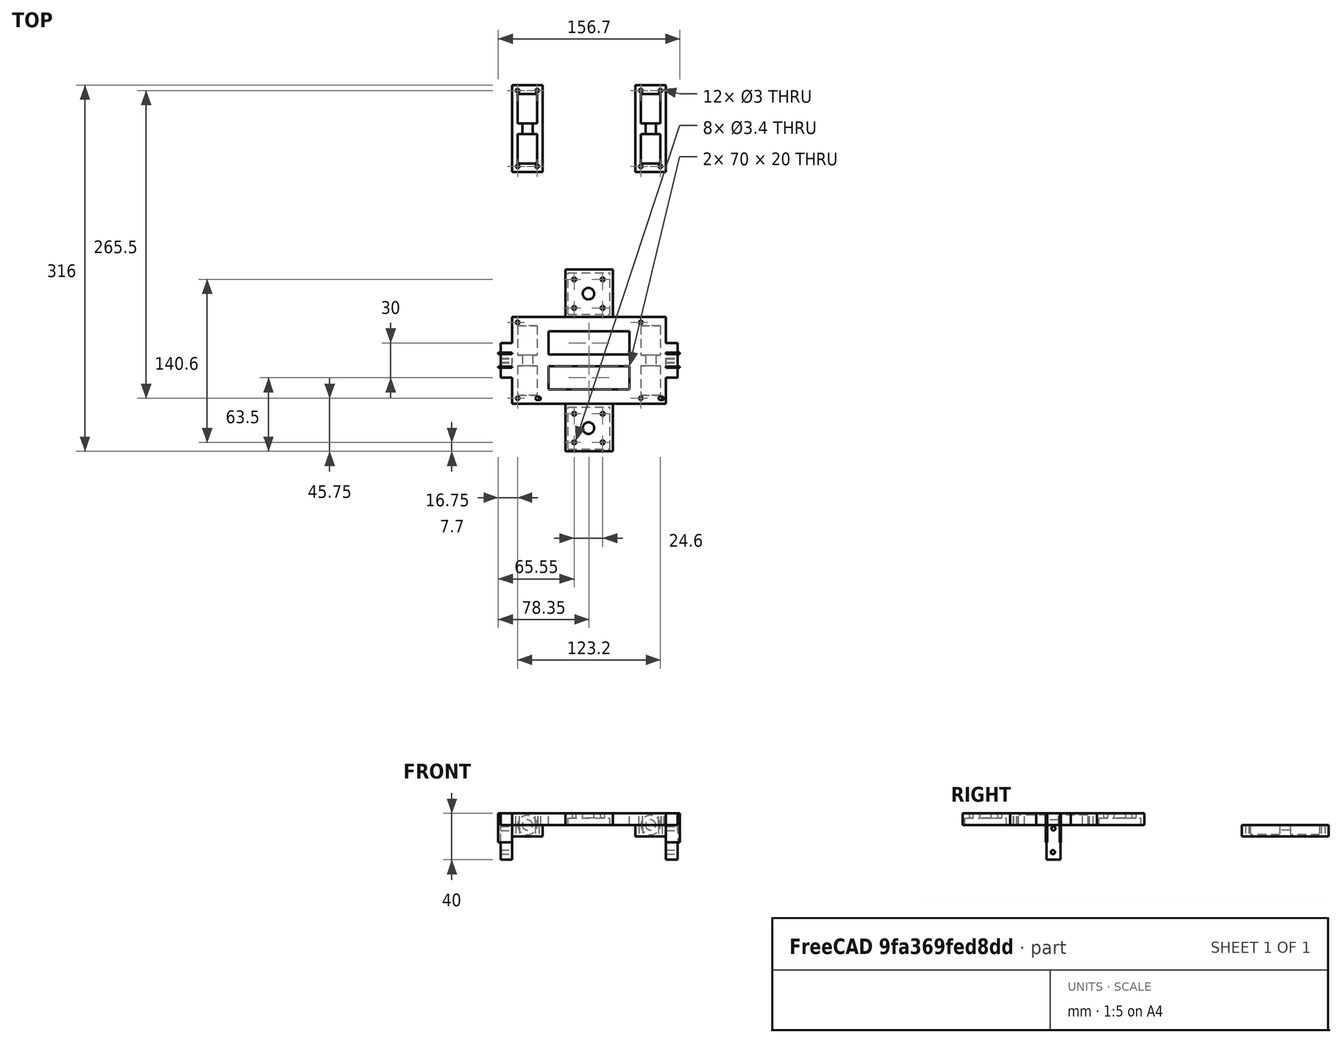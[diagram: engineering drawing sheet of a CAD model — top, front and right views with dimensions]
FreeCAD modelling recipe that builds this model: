
FCSTD DOCUMENT  (FreeCAD 0.16R6712 (Git))
Label: 1
License: All rights reserved
LicenseURL: http://en.wikipedia.org/wiki/All_rights_reserved
objects: Part::Cut×24, Part::Cylinder×21, Part::Box×14, Part::Fuse×5, Part::FeaturePython×4, Part::MultiFuse×3
note: 71 computed .brp shape members not serialized (recipe doc carries the construction recipe); baked Part::Feature solids carry a one-line shape summary decoded from their .brp

FEATURE [Part::Box] Box  label="Cubo"
  Height = 10
  Length = 26.35
  Width = 75
FEATURE [Part::Cylinder] Cylinder  label="Cilindro"
  Angle = 360
  Height = 10
  Placement = pos=(4.75,4.75,0) rot=(0,0,1;0rad)
  Radius = 1.5
FEATURE [Part::Cylinder] Cylinder002  label="Cilindro002"
  Angle = 360
  Height = 10
  Placement = pos=(4.75,70.25,0) rot=(0,0,1;0rad)
  Radius = 1.5
FEATURE [Part::Cylinder] Cylinder003  label="Cilindro003"
  Angle = 360
  Height = 10
  Placement = pos=(23.1425,4.56262,6.40077e-06) rot=(0,0,1;0rad)
  Radius = 1.5
FEATURE [Part::Cut] Cut
  Base = -> Box
  Tool = -> Cylinder
FEATURE [Part::Cut] Cut001
  Base = -> Cut
  Tool = -> Cylinder002
FEATURE [Part::Cut] Cut002
  Base = -> Cut001
  Tool = -> Cylinder003
FEATURE [Part::Cylinder] Cylinder004  label="Cilindro004"
  Angle = 360
  Height = 25.35
  Placement = pos=(13.175,30,0) rot=(1,0,0;1.5708rad)
  Radius = 8.4
FEATURE [Part::Cylinder] Cylinder005  label="Cilindro005"
  Angle = 360
  Height = 25.35
  Placement = pos=(13.175,64.5,0) rot=(1,0,0;1.5708rad)
  Radius = 8.4
FEATURE [Part::Cylinder] Cylinder006  label="Cilindro006"
  Angle = 360
  Height = 9.5
  Placement = pos=(13.175,39.5,0) rot=(1,0,0;1.5708rad)
  Radius = 4.4
FEATURE [Part::Fuse] Fusion
  Base = -> Cylinder004
  Tool = -> Cylinder005
FEATURE [Part::Fuse] Fusion001
  Base = -> Fusion
  Placement = pos=(0,2.75,0) rot=(0,0,1;0rad)
  Tool = -> Cylinder006
FEATURE [Part::Cylinder] Cylinder001  label="Cilindro001"
  Angle = 360
  Height = 10
  Placement = pos=(21.6,4.75,0) rot=(0,0,1;0rad)
  Radius = 1.5
FEATURE [Part::Cut] Cut004
  Base = -> Cut002
  Tool = -> Cylinder001
FEATURE [Part::Cut] Cut003
  Base = -> Cut002
  Tool = -> Cylinder001
FEATURE [Part::Fuse] Fusion002
  Base = -> Cut004
  Tool = -> Cut003
FEATURE [Part::Cut] Cut005
  Base = -> Fusion002
  Tool = -> Fusion001
FEATURE [Part::Cut] Cut006
  Base = -> Cut005
  Tool = -> Cylinder001
FEATURE [Part::FeaturePython] Array  label="Carrileras"  # Draft array (typed FeaturePython)
  Angle = 360
  ArrayType = 0
  Axis = (0,0,1)
  Base = -> Cut006
  Center = (0,0,0)
  Fuse = false
  IntervalAxis = (0,0,0)
  IntervalX = (106.35,0,0)
  IntervalY = (0,1,0)
  IntervalZ = (0,0,0)
  NumberPolar = 1
  NumberX = 2
  NumberY = 1
  NumberZ = 1
FEATURE [Part::Box] Box001  label="Centro"
  Height = 10
  Length = 80
  Placement = pos=(26.35,0,0) rot=(0,0,1;0rad)
  Width = 75
FEATURE [Part::Box] Box002  label="Lucernario"
  Height = 10
  Length = 70
  Placement = pos=(31.35,12.5,0) rot=(0,0,1;0rad)
  Width = 20
FEATURE [Part::Box] Box003  label="Lucernario2"
  Height = 10
  Length = 70
  Placement = pos=(31.35,42.5,0) rot=(0,0,1;0rad)
  Width = 20
FEATURE [Part::Cut] Cut007
  Base = -> Box001
  Tool = -> Box002
FEATURE [Part::Cut] Cut008  label="Centro1"
  Base = -> Cut007
  Tool = -> Box003
FEATURE [Part::Box] Box006  label="Guia1"
  Height = 10
  Length = 10
  Placement = pos=(-10,22.5,0) rot=(0,0,1;0rad)
  Width = 30
FEATURE [Part::Box] Box007  label="Guia2"
  Height = 10
  Length = 10
  Placement = pos=(132.7,22.5,0) rot=(0,0,1;0rad)
  Width = 30
FEATURE [Part::Fuse] Fusion005
  Base = -> Array
  Tool = -> Box006
FEATURE [Part::MultiFuse] Fusion006  label="Carrileras y guias"
  Shapes = -> [Fusion005,Box007]
FEATURE [Part::Box] Box010  label="Cubo003"
  Height = 10
  Length = 26.35
  Width = 75
FEATURE [Part::Cylinder] Cylinder007  label="Cilindro007"
  Angle = 360
  Height = 25.35
  Placement = pos=(13.175,67.25,0) rot=(1,0,0;1.5708rad)
  Radius = 8.4
FEATURE [Part::Cut] Cut011
  Base = -> Box010
  Tool = -> Cylinder007
FEATURE [Part::Cylinder] Cylinder008  label="Cilindro008"
  Angle = 360
  Height = 9.5
  Placement = pos=(13.175,42.25,0) rot=(1,0,0;1.5708rad)
  Radius = 4.4
FEATURE [Part::Cut] Cut012
  Base = -> Cut011
  Tool = -> Cylinder008
FEATURE [Part::Cylinder] Cylinder009  label="Cilindro009"
  Angle = 360
  Height = 25.35
  Placement = pos=(13.175,32.75,0) rot=(1,0,0;1.5708rad)
  Radius = 8.4
FEATURE [Part::Cut] Cut013
  Base = -> Cut012
  Tool = -> Cylinder009
FEATURE [Part::Cylinder] Cylinder010  label="Cilindro010"
  Angle = 360
  Height = 10
  Placement = pos=(21.6,4.75,0) rot=(0,0,1;0rad)
  Radius = 1.5
FEATURE [Part::Cylinder] Cylinder011  label="Cilindro011"
  Angle = 360
  Height = 10
  Placement = pos=(4.75,4.75,0) rot=(0,0,1;0rad)
  Radius = 1.5
FEATURE [Part::Cut] Cut014
  Base = -> Cut013
  Tool = -> Cylinder010
FEATURE [Part::Cut] Cut015
  Base = -> Cut014
  Tool = -> Cylinder011
FEATURE [Part::Cylinder] Cylinder012  label="Cilindro012"
  Angle = 360
  Height = 10
  Placement = pos=(4.75,70.25,0) rot=(0,0,1;0rad)
  Radius = 1.5
FEATURE [Part::Cylinder] Cylinder013  label="Cilindro013"
  Angle = 360
  Height = 10
  Placement = pos=(21.6,70.25,0) rot=(0,0,1;0rad)
  Radius = 1.5
FEATURE [Part::Cut] Cut016
  Base = -> Cut015
  Tool = -> Cylinder012
FEATURE [Part::Cut] Cut017
  Base = -> Cut016
  Placement = pos=(0,0,0) rot=(0,1,0;3.14159rad)
  Tool = -> Cylinder013
FEATURE [Part::FeaturePython] Array001  label="Cierres"  # Draft array (typed FeaturePython)
  Angle = 360
  ArrayType = 0
  Axis = (0,0,1)
  Base = -> Cut017
  Center = (0,0,0)
  Fuse = false
  IntervalAxis = (0,0,0)
  IntervalX = (106.35,0,0)
  IntervalY = (0,1,0)
  IntervalZ = (0,0,0)
  NumberPolar = 1
  NumberX = 2
  NumberY = 1
  NumberZ = 1
  Placement = pos=(26.35,200,0) rot=(0,0,1;0rad)
FEATURE [Part::Box] Box011  label="Cubo004"
  Height = 10
  Length = 41
  Width = 41
FEATURE [Part::Cylinder] Cylinder014  label="Cilindro014"
  Angle = 360
  Height = 10
  Placement = pos=(7.7,7.7,0) rot=(0,0,1;0rad)
  Radius = 1.7
FEATURE [Part::Cylinder] Cylinder015  label="Cilindro015"
  Angle = 360
  Height = 10
  Placement = pos=(7.7,32.3,0) rot=(0,0,1;0rad)
  Radius = 1.7
FEATURE [Part::Cylinder] Cylinder016  label="Cilindro016"
  Angle = 360
  Height = 10
  Placement = pos=(32.3,7.7,0) rot=(0,0,1;0rad)
  Radius = 1.7
FEATURE [Part::Cylinder] Cylinder017  label="Cilindro017"
  Angle = 360
  Height = 10
  Placement = pos=(32.3,32.3,0) rot=(0,0,1;0rad)
  Radius = 1.7
FEATURE [Part::Cylinder] Cylinder018  label="Cilindro018"
  Angle = 360
  Height = 10
  Placement = pos=(20,20,0) rot=(0,0,1;0rad)
  Radius = 5
FEATURE [Part::Cut] Cut018
  Base = -> Box011
  Tool = -> Cylinder015
FEATURE [Part::Cut] Cut019
  Base = -> Cut018
  Tool = -> Cylinder014
FEATURE [Part::Cut] Cut020
  Base = -> Cut019
  Tool = -> Cylinder016
FEATURE [Part::Cut] Cut021
  Base = -> Cut020
  Tool = -> Cylinder017
FEATURE [Part::Cut] Cut022
  Base = -> Cut021
  Tool = -> Cylinder018
FEATURE [Part::Box] Box012  label="Cubo005"
  Height = 6
  Length = 36
  Placement = pos=(2.5,2,0) rot=(0,0,1;0rad)
  Width = 36
FEATURE [Part::Cut] Cut023
  Base = -> Cut022
  Placement = pos=(43.35,-46,0) rot=(0,0,1;0rad)
  Tool = -> Box012
FEATURE [Part::FeaturePython] Array002  # Draft array (typed FeaturePython)
  Angle = 360
  ArrayType = 0
  Axis = (0,0,1)
  Base = -> Cut023
  Center = (0,0,0)
  Fuse = false
  IntervalAxis = (0,0,0)
  IntervalX = (1,0,0)
  IntervalY = (0,116,0)
  IntervalZ = (0,0,0)
  NumberPolar = 1
  NumberX = 1
  NumberY = 2
  NumberZ = 1
  Placement = pos=(2.5,5,0) rot=(0,0,1;0rad)
FEATURE [Part::Fuse] Fusion007
  Base = -> Cut008
  Tool = -> Fusion006
FEATURE [Part::Box] Box014  label="Cubo007"
  Height = 25
  Length = 12
  Placement = pos=(132.7,31,-15) rot=(0,0,1;0rad)
  Width = 1
FEATURE [Part::Box] Box015  label="Cubo008"
  Height = 25
  Length = 12
  Placement = pos=(132.7,43,-15) rot=(0,0,1;0rad)
  Width = 1
FEATURE [Part::Box] Box016  label="Cubo009"
  Height = 30
  Length = 10
  Placement = pos=(-10,31.5,-30) rot=(0,0,1;0rad)
  Width = 12
FEATURE [Part::Box] Box017  label="Cubo010"
  Height = 25
  Length = 12
  Placement = pos=(-12,31,-15) rot=(0,0,1;0rad)
  Width = 1
FEATURE [Part::Box] Box018  label="Cubo011"
  Height = 25
  Length = 12
  Placement = pos=(-12,43,-15) rot=(0,0,1;0rad)
  Width = 1
FEATURE [Part::Cylinder] Cylinder019  label="Cilindro019"
  Angle = 360
  Height = 10
  Placement = pos=(-10,37.5,-3) rot=(0,1,0;1.5708rad)
  Radius = 1.75
FEATURE [Part::Cylinder] Cylinder020  label="Cilindro020"
  Angle = 360
  Height = 10
  Placement = pos=(-10,37,-23.5) rot=(0,1,0;1.5708rad)
  Radius = 1.75
FEATURE [Part::Cut] Cut024
  Base = -> Box016
  Tool = -> Cylinder020
FEATURE [Part::Cut] Cut025
  Base = -> Cut024
  Tool = -> Cylinder019
FEATURE [Part::FeaturePython] Array003  # Draft array (typed FeaturePython)
  Angle = 360
  ArrayType = 0
  Axis = (0,0,1)
  Base = -> Cut025
  Center = (0,0,0)
  Fuse = false
  IntervalAxis = (0,0,0)
  IntervalX = (142.7,0,0)
  IntervalY = (0,1,0)
  IntervalZ = (0,0,0)
  NumberPolar = 1
  NumberX = 2
  NumberY = 1
  NumberZ = 1
FEATURE [Part::MultiFuse] Fusion009
  Shapes = -> [Box015,Box014,Array003]
FEATURE [Part::MultiFuse] Fusion010
  Shapes = -> [Fusion009,Box018,Box017]
